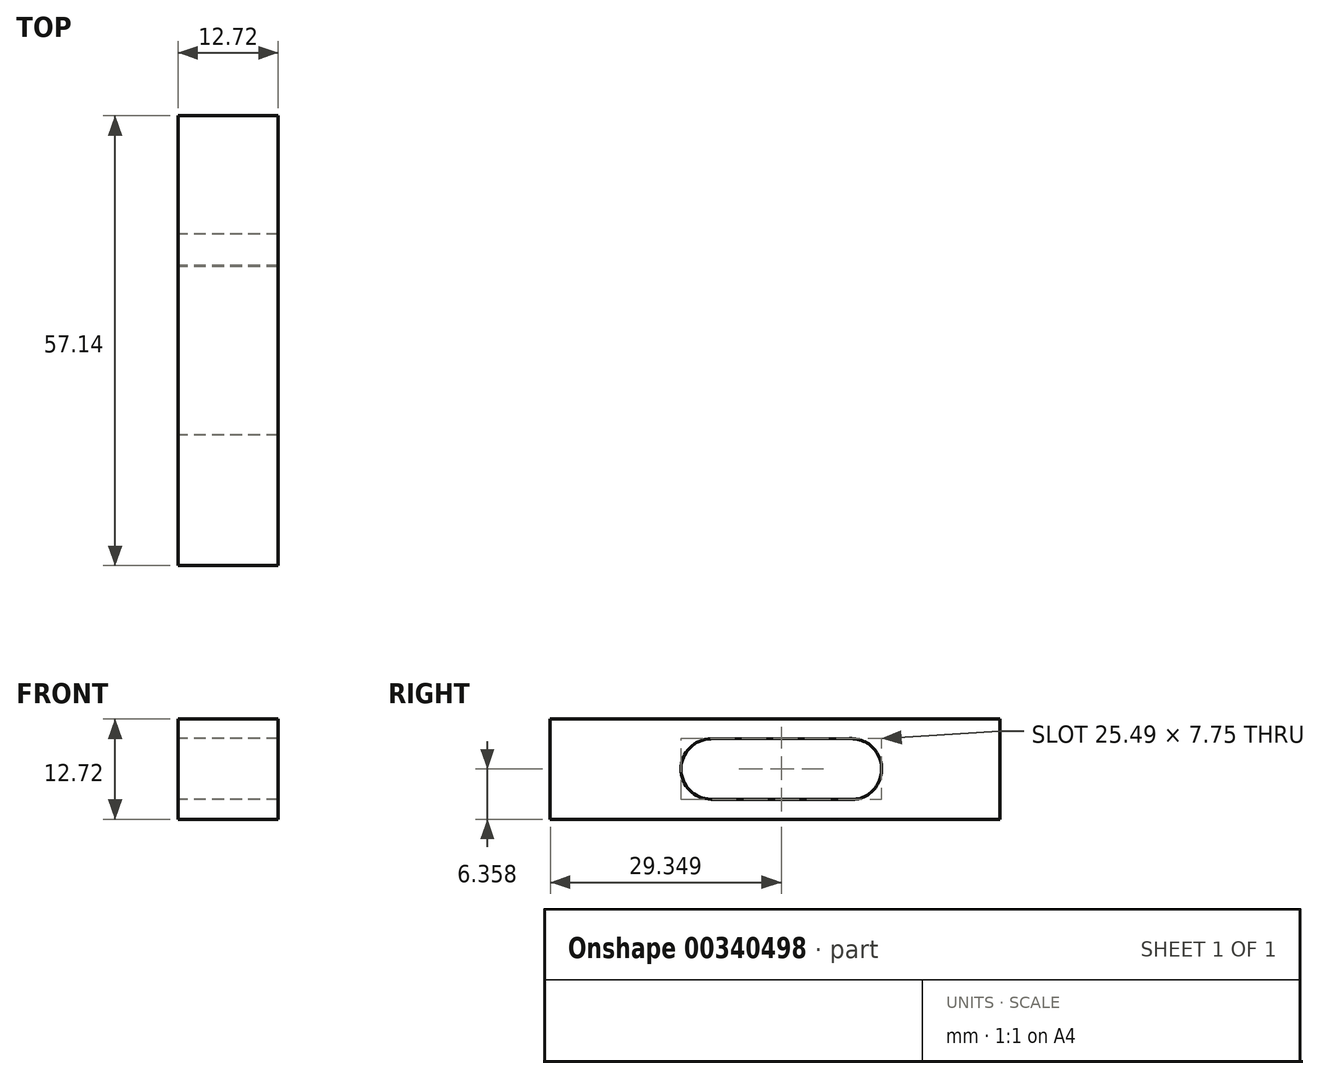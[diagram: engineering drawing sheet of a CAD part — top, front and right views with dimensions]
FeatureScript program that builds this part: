
annotation { "Feature Type Name" : "Feature", "Feature Type Description" : "" }
export const myFeature = defineFeature(function(context is Context, id is Id, definition is map)
    precondition{}
    {
        {
            var Q0;
            Q0=qCreatedBy(makeId("Front.planeOp"),FACE);
            var sketch = newSketch(context, id + "F0", { "sketchPlane" : qUnion([Q0])});
            skLineSegment(sketch, "E0.bottom", {"start": v(6.36, -6.36) * mm, "end": v(-6.36, -6.36) * mm});
            skLineSegment(sketch, "E0.top", {"start": v(6.36, 6.36) * mm, "end": v(-6.36, 6.36) * mm});
            skLineSegment(sketch, "E0.left", {"start": v(6.36, -6.36) * mm, "end": v(6.36, 6.36) * mm});
            skLineSegment(sketch, "E0.right", {"start": v(-6.36, -6.36) * mm, "end": v(-6.36, 6.36) * mm});
            skPoint(sketch, "E0.middle", {"position": v(0, 0) * mm});
            skSolve(sketch);
        }
        {
            var Q0;
            Q0=makeQuery(id+"F0.imprint","IMPRINT",FACE,{"disambiguationData":[TD([[makeQuery(id+"F0.imprint","IMPRINT",EDGE,{"derivedFrom":sQuery(id+"F0.wireOp",EDGE,"E0.bottom")}),-1.0]])]});
            extrude(context, id + "F1", {"entities" : qUnion([Q0]), "endBound" : BoundingType.SYMMETRIC, "depth" : 57.15 * mm});
        }
        {
            var Q0;
            Q0=makeQuery(id+"F1.opExtrude","SWEPT_FACE",FACE,{"disambiguationData":[OSD([sQuery(id+"F0.wireOp",EDGE,"E0.right")])]});
            var sketch = newSketch(context, id + "F2", { "sketchPlane" : qUnion([Q0])});
            skCircle(sketch, "E1", {"center": v(-9.65, 0) * mm, "radius": 3.88 * mm});
            skCircle(sketch, "E2", {"center": v(8.14, 0) * mm, "radius": 3.83 * mm});
            skLineSegment(sketch, "E3", {"start": v(-9.43, 3.87) * mm, "end": v(8.14, 3.83) * mm});
            skLineSegment(sketch, "E4", {"start": v(-9.54, -3.88) * mm, "end": v(8.14, -3.83) * mm});
            skSolve(sketch);
        }
        {
            var Q0;
            {var subQ0=sQuery(id+"F2.wireOp",EDGE,"E3");Q0=makeQuery(id+"F2.imprint","IMPRINT",FACE,{"disambiguationData":[TD([[makeQuery(id+"F2.imprint","IMPRINT",EDGE,{"derivedFrom":subQ0}),-1.0]])]});}
            var Q1;
            {var subQ0=sQuery(id+"F2.wireOp",EDGE,"E2");var subQ1=makeQuery(id+"F2.imprint","INTERSECT",VERTEX,{"derivedFrom":[subQ0,sQuery(id+"F2.wireOp",EDGE,"E3")]});Q1=makeQuery(id+"F2.imprint","IMPRINT",FACE,{"disambiguationData":[TD([[makeQuery(id+"F2.imprint","IMPRINT",EDGE,{"disambiguationData":[TD([[subQ1,-1.0]])],"derivedFrom":subQ0}),1.0]])]});}
            var Q2;
            {var subQ0=sQuery(id+"F2.wireOp",EDGE,"E1");var subQ1=makeQuery(id+"F2.imprint","INTERSECT",VERTEX,{"derivedFrom":[subQ0,sQuery(id+"F2.wireOp",EDGE,"E3")]});Q2=makeQuery(id+"F2.imprint","IMPRINT",FACE,{"disambiguationData":[TD([[makeQuery(id+"F2.imprint","IMPRINT",EDGE,{"disambiguationData":[TD([[subQ1,-1.0]])],"derivedFrom":subQ0}),1.0]])]});}
            extrude(context, id + "F3", {"entities" : qUnion([Q0, Q1, Q2]), "operationType" : NewBodyOperationType.REMOVE, "endBound" : BoundingType.UP_TO_NEXT, "oppositeDirection" : true, "depth" : 25.4 * mm});
        }
    });
